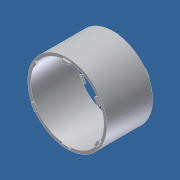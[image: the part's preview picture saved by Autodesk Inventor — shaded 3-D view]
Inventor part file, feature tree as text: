
AUTODESK INVENTOR PART (.ipt)
format: ipt  version: unknown  size: 227,328 bytes
history: native  units: in
note: dims shown in document units (in); Inventor stores cm internally (conversion verified against a paired STEP export)
features: extrude x2, sketch x2, pattern_circular x1, pattern_linear x1
ambient origin geometry x8: Origin, YZ Plane, XZ Plane, XY Plane, X Axis, Y Axis, Z Axis, Center Point
bodies: Solid1 (feature_tree)
feature tree (6):
  extrude  "Extrusion1"  Depth=2.05in TaperAngle=0.0deg
  extrude  "Extrusion4"  Depth=0.32in
  pattern_circular  "Circular Pattern1"  [2 undecoded]
  pattern_linear  "Rectangular Pattern1"  Spacing1=1.585in  [1 undecoded]
  sketch  "Sketch1"  dims[d0=3.55in d2=2.05in d3=0.0in]
  sketch  "Sketch2"  dims[d4=0.103in d5=0.32in d38=0.1365in d39=1.585in d40=0.088in d41=0.0in d42=2.3622in d43=360.0deg d45=0.7874in d47=2.138in]
note: 3 required parameter values undecoded (feature->parameter linkage not recoverable at this tier; creation-order binding heuristic only, values carry confidence <= 0.55)
